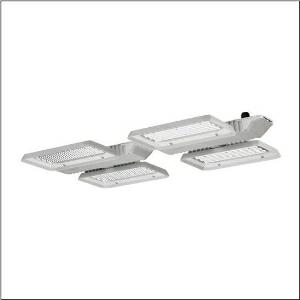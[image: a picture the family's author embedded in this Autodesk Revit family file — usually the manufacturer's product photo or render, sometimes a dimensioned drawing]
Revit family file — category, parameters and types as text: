
# Revit family: highbay_21_51hla1d24mcb
name_source: partatom
category: Lighting Fixtures
units: mm (PartAtom-declared; Revit-internal decimal feet)

## family parameters
Cut with Voids When Loaded = No
Host = Face
Light Source = No
Part Type = Normal
Room Calculation Point = No
Round Connector Dimension = Use Diameter
Shared = No

## types (1)
- --- (1 x LED, 26940 lm, 171.1 W, 4000K)
    Apparent Load = 171 VA
    CIE Flux Codes = 88 95 99 100 99
    Color Rendering = 80
    Color Temperature = 4000K
    Default Elevation = 1800 mm
    Description = Highbay 21, LED high bay luminaire, primary light control with lens, of PMMA, light emission: direct distribution, primary light characteristic: symmetric, installation type: suspended mounting, surface-mounted, for 2x 2 x LED rated luminous flux: 26.940 lm, light colour: 840, colour temperature: 4000K, control gear: ECG DALI, with terminal, 5-pole, max. 2.5mm², mains connection: 230..240V, AC, 50/60Hz, rated input power: 171W, LED unit, of diecast aluminium, unplated, bead blasted, silver, length: 940 mm, width: 500 mm, height: 65mm, housing, of diecast aluminium, uncoated, bead blasted, silver, protection rating (complete): IP65, insulation class (complete): insulation class I (protective earthing), certification: CE, ENEC, VDE, protection symbol: D, impact resistance: IK08 with glass or PC cover, permissible ambient temperature for indoor applications: -35..+45°C, corresponds to IFS (International Featured Standards) requirements for safety and quality in the food industry, reducing of maximum allowable ambient temperature of 5°C with ceiling mounting, packaging unit: 1 piece
    Height = 95 mm
    Lamp = 1 x LED
    Lamp Light Flux = 26940 lm
    Lamp Power = 171.1 W
    Lamp count = 1
    Length = 939 mm
    Luminous efficacy = 157 lm/W
    Manufacturer = Siteco
    ModVariant = No
    Model = 51HLA1D24MCB
    Mounting Place = Ceiling
    Mounting Type = Pendant
    Number of Poles = 1
    OnlyDefault = Yes
    Power Factor = 1
    Product Name = Highbay 21
    Product group = LED high bay luminaire
    ProductGroupID = 903
    Protection Class = Protection class I
    Protection Degree = IP 65
    RLX_Detail_Level = 1
    RlxData = <blob elided: 64501 chars, md5=0dae8ac4>
    Socket = socket
    Standby Power = 0 W
    System Light Flux = 26940 lm
    System Power = 171 W
    Type Comments = factory setting: luminous flux: 100 % | dim-lin: 254 | 490 mA
    Type Image = l_1003428.jpg
    URL = http://relux.com
    VarID = @adj_135855
    Voltage = 0 V
    Weight = 0.00 kg
    Width = 501 mm

## geometry (parser evidence)
native form markers: Blend x4, Sweep x11
no freeform markers — native parametric forms only
